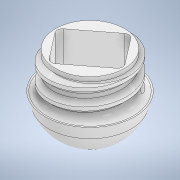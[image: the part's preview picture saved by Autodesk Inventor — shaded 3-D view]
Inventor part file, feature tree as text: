
AUTODESK INVENTOR PART (.ipt)
format: ipt  version: 2020 (Build 240168000, 168)  size: 738,304 bytes
history: native  units: in
note: dims shown in document units (in); Inventor stores cm internally (conversion verified against a paired STEP export)
features: other x6, sketch x5, thread x2, revolve x2, helix x2, emboss x2, shell x1, boolean_combine x1, extrude x1
ambient origin geometry x8: Origin, YZ Plane, XZ Plane, XY Plane, X Axis, Y Axis, Z Axis, Center Point
bodies: Solid1 (feature_tree), Solid2 (feature_tree), Solid3 (feature_tree)
feature tree (22):
  other  "SmartEgg Housing Main.ipt"
  other  "SmartEgg Housing Cap.ipt"
  shell  "Shell Sketch"  Thickness=0.3937in
  thread  "Thread Sketch"  [1 undecoded]
  revolve  "Revolution1"  [1 undecoded]
  helix  "Coil1"  [1 undecoded]
  helix  "Coil2"  [1 undecoded]
  thread  "Thread Mask"  [1 undecoded]
  revolve  "Revolution4"  [1 undecoded]
  boolean_combine  "Combine1"
  sketch  "Sketch10"  dims[d23=0.0787in d24=0.4921in]
  sketch  "Sketch11"  dims[d25=0.0098in d26=0.7874in]
  extrude  "Extrusion1"  Depth=0.7874in
  other  "Vent Lookup"
  other  "Vent Plane"
  emboss  "Emboss1"
  emboss  "Emboss2"
  sketch  "Sketch3"  dims[d18=0.9843in d19=1.9685in d20=0.0394in d21=0.6693in d22=0.1969in]
  other  "Housing Largest Area"
  other  "ESP32 Feather"
  sketch  "Sketch13"  dims[d27=0.1181in]
  sketch  "Sketch14"  dims[d28=0.0787in d29=2.7769in d30=0.0394in d32=0.0197in d33=0.0197in d35=45.0deg d36=0.0197in d37=0.0787in d38=0.0787in d39=0.2756in d40=90.0deg d41=0.3706in d42=0.3937in d43=1.1811in d44=0.0in d45=90.0deg d46=90.0deg d47=0.0in d48=0.0in d50=0.3706in d51=0.3937in d52=0.3937in d53=0.0in d54=90.0deg d55=90.0deg d56=0.0in d57=0.0in d61=0.0984in d62=90.0deg d64=0.0148in d65=1.2106in d66=0.1181in d67=1.3976in d68=1.3976in d69=0.0in d71=0.2559in d72=1.9488in d73=0.0154in d74=0.0in d75=0.0787in d76=0.0787in d77=0.0787in d78=0.0394in d79=0.0in d82=0.1969in]
note: 6 required parameter values undecoded (feature->parameter linkage not recoverable at this tier; creation-order binding heuristic only, values carry confidence <= 0.55)